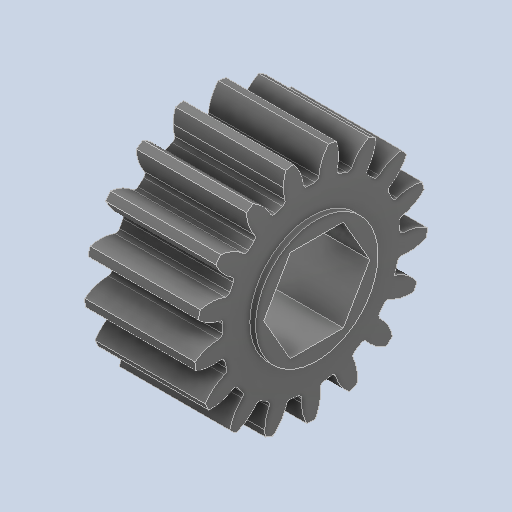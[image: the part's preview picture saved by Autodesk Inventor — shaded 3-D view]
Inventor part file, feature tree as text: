
AUTODESK INVENTOR PART (.ipt)
format: ipt  version: 2023.2 (Build 272271000, 271)  size: 289,792 bytes
history: native  units: in
note: dims shown in document units (in); Inventor stores cm internally (conversion verified against a paired STEP export)
features: fillet x1
ambient origin geometry x8: Origin, YZ Plane, XZ Plane, XY Plane, X Axis, Y Axis, Z Axis, Center Point
bodies: Solid1 (feature_tree)
feature tree (1):
  fillet  "Fillet1"  [1 undecoded]
note: 1 required parameter value undecoded (feature->parameter linkage not recoverable at this tier; creation-order binding heuristic only, values carry confidence <= 0.55)
